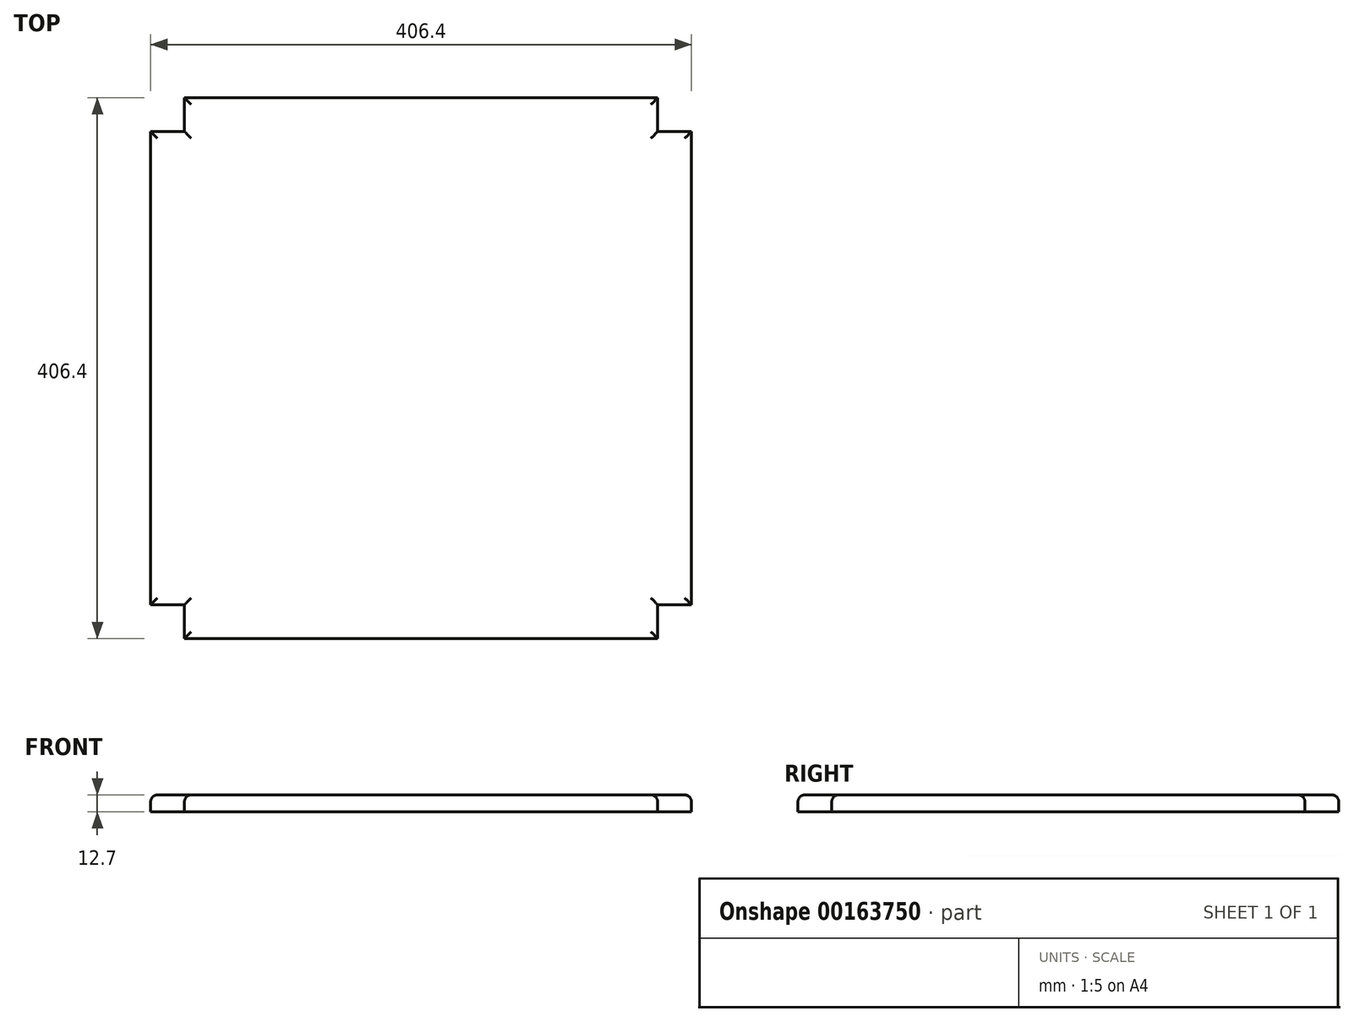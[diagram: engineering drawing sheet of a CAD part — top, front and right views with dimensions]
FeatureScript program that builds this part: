
annotation { "Feature Type Name" : "Feature", "Feature Type Description" : "" }
export const myFeature = defineFeature(function(context is Context, id is Id, definition is map)
    precondition{}
    {
        {
            var Q0;
            Q0=qCreatedBy(makeId("Top.planeOp"),FACE);
            var sketch = newSketch(context, id + "F0", { "sketchPlane" : qUnion([Q0])});
            skLineSegment(sketch, "E0.bottom", {"start": v(-177.8, 135.47) * mm, "end": v(177.8, 135.47) * mm});
            skLineSegment(sketch, "E0.top", {"start": v(-177.8, -270.93) * mm, "end": v(177.8, -270.93) * mm});
            skLineSegment(sketch, "E0.left", {"start": v(-203.2, 110.07) * mm, "end": v(-203.2, -245.53) * mm});
            skLineSegment(sketch, "E0.right", {"start": v(203.2, 110.07) * mm, "end": v(203.2, -245.53) * mm});
            skPoint(sketch, "E0.middle", {"position": v(0, 0) * mm});
            skPoint(sketch, "E1.visualSharp", {"position": v(-203.2, 135.47) * mm});
            skLineSegment(sketch, "E2.top", {"start": v(-203.2, -245.53) * mm, "end": v(-177.8, -245.53) * mm});
            skLineSegment(sketch, "E2.right", {"start": v(-177.8, -270.93) * mm, "end": v(-177.8, -245.53) * mm});
            skLineSegment(sketch, "E3.top", {"start": v(-203.2, 110.07) * mm, "end": v(-177.8, 110.07) * mm});
            skLineSegment(sketch, "E3.right", {"start": v(-177.8, 135.47) * mm, "end": v(-177.8, 110.07) * mm});
            skLineSegment(sketch, "E4.top", {"start": v(203.2, 110.07) * mm, "end": v(177.8, 110.07) * mm});
            skLineSegment(sketch, "E4.right", {"start": v(177.8, 135.47) * mm, "end": v(177.8, 110.07) * mm});
            skLineSegment(sketch, "E5.top", {"start": v(203.2, -245.53) * mm, "end": v(177.8, -245.53) * mm});
            skLineSegment(sketch, "E5.right", {"start": v(177.8, -270.93) * mm, "end": v(177.8, -245.53) * mm});
            skSolve(sketch);
        }
        {
            var Q0;
            Q0=qSketchRegion(id+"F0",true);
            extrude(context, id + "F1", {"entities" : qUnion([Q0]), "depth" : 12.7 * mm});
        }
        {
            var Q0;
            Q0=makeQuery(id+"F1.opExtrude","CAP_EDGE",EDGE,{"disambiguationData":[OSD([sQuery(id+"F0.wireOp",EDGE,"E0.left")])],"isStart":false});
            var Q1;
            Q1=makeQuery(id+"F1.opExtrude","CAP_EDGE",EDGE,{"disambiguationData":[OSD([sQuery(id+"F0.wireOp",EDGE,"E0.top")])],"isStart":false});
            var Q2;
            Q2=makeQuery(id+"F1.opExtrude","CAP_EDGE",EDGE,{"disambiguationData":[OSD([sQuery(id+"F0.wireOp",EDGE,"E0.right")])],"isStart":false});
            var Q3;
            Q3=makeQuery(id+"F1.opExtrude","CAP_EDGE",EDGE,{"disambiguationData":[OSD([sQuery(id+"F0.wireOp",EDGE,"E0.bottom")])],"isStart":false});
            var Q4;
            Q4=makeQuery(id+"F1.opExtrude","CAP_EDGE",EDGE,{"disambiguationData":[OSD([sQuery(id+"F0.wireOp",EDGE,"E3.top")])],"isStart":false});
            var Q5;
            Q5=makeQuery(id+"F1.opExtrude","CAP_EDGE",EDGE,{"disambiguationData":[OSD([sQuery(id+"F0.wireOp",EDGE,"E3.right")])],"isStart":false});
            var Q6;
            Q6=makeQuery(id+"F1.opExtrude","CAP_EDGE",EDGE,{"disambiguationData":[OSD([sQuery(id+"F0.wireOp",EDGE,"E4.right")])],"isStart":false});
            var Q7;
            Q7=makeQuery(id+"F1.opExtrude","CAP_EDGE",EDGE,{"disambiguationData":[OSD([sQuery(id+"F0.wireOp",EDGE,"E4.top")])],"isStart":false});
            var Q8;
            Q8=makeQuery(id+"F1.opExtrude","CAP_EDGE",EDGE,{"disambiguationData":[OSD([sQuery(id+"F0.wireOp",EDGE,"E2.top")])],"isStart":false});
            var Q9;
            Q9=makeQuery(id+"F1.opExtrude","CAP_EDGE",EDGE,{"disambiguationData":[OSD([sQuery(id+"F0.wireOp",EDGE,"E2.right")])],"isStart":false});
            var Q10;
            Q10=makeQuery(id+"F1.opExtrude","CAP_EDGE",EDGE,{"disambiguationData":[OSD([sQuery(id+"F0.wireOp",EDGE,"E5.right")])],"isStart":false});
            var Q11;
            Q11=makeQuery(id+"F1.opExtrude","CAP_EDGE",EDGE,{"disambiguationData":[OSD([sQuery(id+"F0.wireOp",EDGE,"E5.top")])],"isStart":false});
            fillet(context, id + "F2", {"entities" : qUnion([Q0, Q1, Q2, Q3, Q4, Q5, Q6, Q7, Q8, Q9, Q10, Q11]), "radius" : 5.08 * mm, "tangentPropagation" : true, "allowEdgeOverflow" : false});
        }
    });
